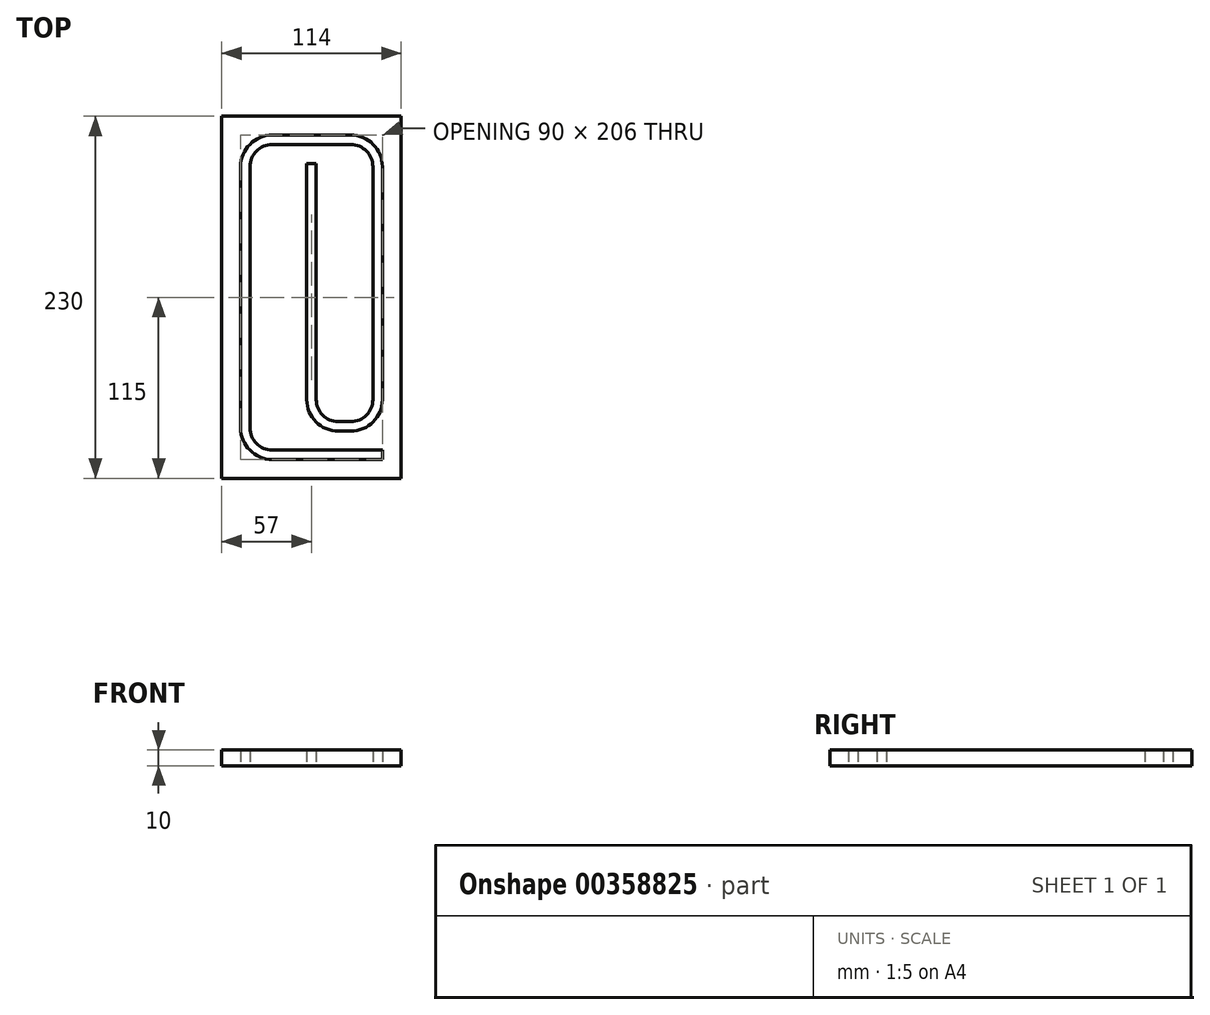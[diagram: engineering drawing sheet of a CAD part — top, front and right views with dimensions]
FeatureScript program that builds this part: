
annotation { "Feature Type Name" : "Feature", "Feature Type Description" : "" }
export const myFeature = defineFeature(function(context is Context, id is Id, definition is map)
    precondition{}
    {
        {
            var Q0;
            Q0=qCreatedBy(makeId("Top.planeOp"),FACE);
            var sketch = newSketch(context, id + "F0", { "sketchPlane" : qUnion([Q0])});
            skLineSegment(sketch, "E0.bottom", {"start": v(0, 230) * mm, "end": v(114, 230) * mm});
            skLineSegment(sketch, "E0.top", {"start": v(0, 0) * mm, "end": v(114, 0) * mm});
            skLineSegment(sketch, "E0.left", {"start": v(0, 230) * mm, "end": v(0, 0) * mm});
            skLineSegment(sketch, "E0.right", {"start": v(114, 230) * mm, "end": v(114, 0) * mm});
            skLineSegment(sketch, "E1.0", {"start": v(12, 198) * mm, "end": v(12, 32) * mm});
            skLineSegment(sketch, "E1.1", {"start": v(32, 218) * mm, "end": v(82, 218) * mm});
            skLineSegment(sketch, "E1.3", {"start": v(32, 12) * mm, "end": v(82, 12) * mm});
            skPoint(sketch, "E2.visualSharp", {"position": v(12, 218) * mm});
            skArc(sketch, "E2.filletArc", {"start": v(32, 218) * mm, "mid": v(17.86, 212.14) * mm, "end": v(12, 198) * mm});
            skPoint(sketch, "E3.visualSharp", {"position": v(102, 218) * mm});
            skArc(sketch, "E3.filletArc", {"start": v(102, 198) * mm, "mid": v(96.14, 212.14) * mm, "end": v(82, 218) * mm});
            skPoint(sketch, "E4.visualSharp", {"position": v(12, 12) * mm});
            skArc(sketch, "E4.filletArc", {"start": v(12, 32) * mm, "mid": v(17.86, 17.86) * mm, "end": v(32, 12) * mm});
            skPoint(sketch, "E5.visualSharp", {"position": v(102, 12) * mm});
            skLineSegment(sketch, "E6.0", {"start": v(18, 198) * mm, "end": v(18, 32) * mm});
            skArc(sketch, "E6.1", {"start": v(32, 212) * mm, "mid": v(22.1, 207.9) * mm, "end": v(18, 198) * mm});
            skArc(sketch, "E6.2", {"start": v(18, 32) * mm, "mid": v(22.1, 22.1) * mm, "end": v(32, 18) * mm});
            skLineSegment(sketch, "E6.3", {"start": v(32, 212) * mm, "end": v(82, 212) * mm});
            skLineSegment(sketch, "E6.4", {"start": v(32, 18) * mm, "end": v(102, 18) * mm});
            skLineSegment(sketch, "E6.6", {"start": v(96, 198) * mm, "end": v(96, 50) * mm});
            skArc(sketch, "E6.7", {"start": v(96, 198) * mm, "mid": v(91.9, 207.9) * mm, "end": v(82, 212) * mm});
            skLineSegment(sketch, "E7", {"start": v(57, 212) * mm, "end": v(57, 200) * mm, "construction": true});
            skLineSegment(sketch, "E8", {"start": v(57, 200) * mm, "end": v(57, 30) * mm, "construction": true});
            skLineSegment(sketch, "E9", {"start": v(57, 30) * mm, "end": v(57, 18) * mm, "construction": true});
            skLineSegment(sketch, "E10.0", {"start": v(54, 200) * mm, "end": v(54, 50) * mm});
            skLineSegment(sketch, "E11.0", {"start": v(60, 200) * mm, "end": v(60, 50) * mm});
            skLineSegment(sketch, "E12", {"start": v(74, 30) * mm, "end": v(82, 30) * mm});
            skLineSegment(sketch, "E13", {"start": v(82, 12) * mm, "end": v(102, 12) * mm});
            skLineSegment(sketch, "E14", {"start": v(102, 50) * mm, "end": v(102, 198) * mm});
            skPoint(sketch, "E15.visualSharp", {"position": v(54, 30) * mm});
            skArc(sketch, "E15.filletArc", {"start": v(54, 50) * mm, "mid": v(59.86, 35.86) * mm, "end": v(74, 30) * mm});
            skArc(sketch, "E16.filletArc", {"start": v(82, 30) * mm, "mid": v(96.14, 35.86) * mm, "end": v(102, 50) * mm});
            skPoint(sketch, "E17.orphan", {"position": v(82, 18) * mm});
            skLineSegment(sketch, "E18", {"start": v(102, 12) * mm, "end": v(102, 18) * mm});
            skArc(sketch, "E19.0", {"start": v(82, 36) * mm, "mid": v(91.9, 40.1) * mm, "end": v(96, 50) * mm});
            skLineSegment(sketch, "E19.1", {"start": v(74, 36) * mm, "end": v(82, 36) * mm});
            skArc(sketch, "E19.2", {"start": v(60, 50) * mm, "mid": v(64.1, 40.1) * mm, "end": v(74, 36) * mm});
            skLineSegment(sketch, "E20", {"start": v(54, 200) * mm, "end": v(60, 200) * mm});
            skSolve(sketch);
        }
        {
            var Q0;
            Q0=makeQuery(id+"F0.imprint","IMPRINT",FACE,{"disambiguationData":[TD([[makeQuery(id+"F0.imprint","IMPRINT",EDGE,{"derivedFrom":sQuery(id+"F0.wireOp",EDGE,"E0.bottom")}),-1.0]])]});
            extrude(context, id + "F1", {"entities" : qUnion([Q0]), "depth" : 10 * mm});
        }
    });
